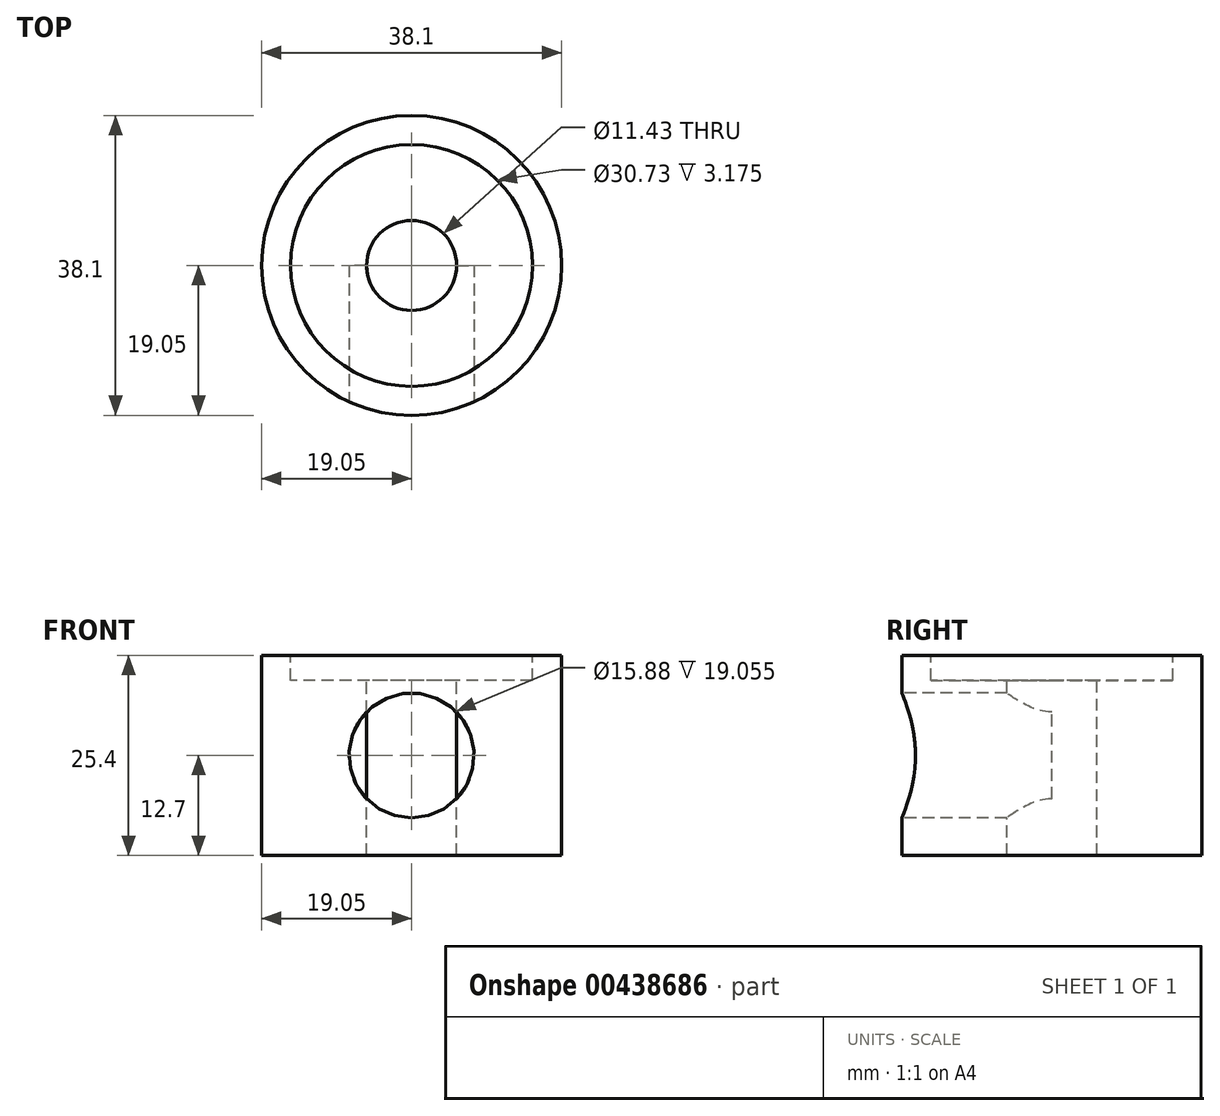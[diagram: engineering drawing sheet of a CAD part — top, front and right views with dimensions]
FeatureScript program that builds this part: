
annotation { "Feature Type Name" : "Feature", "Feature Type Description" : "" }
export const myFeature = defineFeature(function(context is Context, id is Id, definition is map)
    precondition{}
    {
        {
            var Q0;
            Q0=qCreatedBy(makeId("Top.planeOp"),FACE);
            var sketch = newSketch(context, id + "F0", { "sketchPlane" : qUnion([Q0])});
            skCircle(sketch, "E0", {"center": v(0, 0) * mm, "radius": 19.05 * mm});
            skSolve(sketch);
        }
        {
            var Q0;
            Q0=makeQuery(id+"F0.imprint","IMPRINT",FACE,{"disambiguationData":[TD([[makeQuery(id+"F0.imprint","IMPRINT",EDGE,{"derivedFrom":sQuery(id+"F0.wireOp",EDGE,"E0")}),1.0]])]});
            extrude(context, id + "F1", {"entities" : qUnion([Q0]), "depth" : 25.4 * mm});
        }
        {
            var Q0;
            Q0=makeQuery(id+"F1.opExtrude","CAP_FACE",FACE,{"disambiguationData":[OSD([sQuery(id+"F0.wireOp",EDGE,"E0")])],"isStart":false});
            var sketch = newSketch(context, id + "F2", { "sketchPlane" : qUnion([Q0])});
            skPoint(sketch, "E1", {"position": v(0, 0) * mm});
            skSolve(sketch);
        }
        {
            var Q0;
            Q0=sQuery(id+"F2.wireOp",VERTEX,"E1");
            var Q1;
            Q1=makeQuery(id+"F1.opExtrude","SWEPT_BODY",BODY,{"disambiguationData":[OSD([sQuery(id+"F0.wireOp",EDGE,"E0")])]});
            hole(context, id + "F3", {"style" : HoleStyle.SIMPLE, "endStyle" : HoleEndStyle.THROUGH, "holeDiameter" : 11.43 * mm, "isTappedThrough" : true, "tappedDepth" : 12.7 * mm, "tapClearance" : 3, "locations" : qUnion([Q0]), "scope" : qUnion([Q1])});
        }
        {
            var Q0;
            Q0=makeQuery(id+"F1.opExtrude","CAP_FACE",FACE,{"disambiguationData":[OSD([sQuery(id+"F0.wireOp",EDGE,"E0")])],"isStart":false});
            var sketch = newSketch(context, id + "F4", { "sketchPlane" : qUnion([Q0])});
            skCircle(sketch, "E2", {"center": v(0, 0) * mm, "radius": 15.37 * mm});
            skSolve(sketch);
        }
        {
            var Q0;
            Q0=makeQuery(id+"F4.imprint","IMPRINT",FACE,{"disambiguationData":[TD([[makeQuery(id+"F4.imprint","IMPRINT",EDGE,{"derivedFrom":sQuery(id+"F4.wireOp",EDGE,"E2")}),1.0]])]});
            extrude(context, id + "F5", {"entities" : qUnion([Q0]), "operationType" : NewBodyOperationType.REMOVE, "oppositeDirection" : true, "depth" : 3.17 * mm});
        }
        {
            var Q0;
            Q0=qCreatedBy(makeId("Front.planeOp"),FACE);
            cPlane(context, id + "F6", {"entities" : qUnion([Q0]), "cplaneType" : CPlaneType.OFFSET, "offset" : 19.05 * mm, "width" : 152.4 * mm, "height" : 152.4 * mm});
        }
        {
            var Q0;
            Q0=qCreatedBy(id+"F6.planeOp",FACE);
            var sketch = newSketch(context, id + "F7", { "sketchPlane" : qUnion([Q0])});
            skCircle(sketch, "E3", {"center": v(0, 12.7) * mm, "radius": 7.94 * mm});
            skSolve(sketch);
        }
        {
            var Q0;
            Q0=makeQuery(id+"F7.imprint","IMPRINT",FACE,{"disambiguationData":[TD([[makeQuery(id+"F7.imprint","IMPRINT",EDGE,{"derivedFrom":sQuery(id+"F7.wireOp",EDGE,"E3")}),1.0]])]});
            extrude(context, id + "F8", {"entities" : qUnion([Q0]), "operationType" : NewBodyOperationType.REMOVE, "oppositeDirection" : true, "depth" : 19.05 * mm});
        }
    });
